FCSTD DOCUMENT  (FreeCAD 0.18R16146 (Git))
Label: t-1
License: All rights reserved
LicenseURL: http://en.wikipedia.org/wiki/All_rights_reserved
objects: Sketcher::SketchObject×1, PartDesign::Body×1
note: 2 computed .brp shape members not serialized (recipe doc carries the construction recipe); baked Part::Feature solids carry a one-line shape summary decoded from their .brp

FEATURE [Sketcher::SketchObject] Sketch
  MapMode = 5
  Support = -> [XY_Plane]
  sketch-geometry (9):
    g0: LineSegment StartX=0 StartY=0 StartZ=0 EndX=100 EndY=0 EndZ=0
    g1: LineSegment StartX=100 StartY=0 StartZ=0 EndX=100 EndY=33 EndZ=0
    g2: LineSegment StartX=100 StartY=33 StartZ=0 EndX=0 EndY=33 EndZ=0
    g3: LineSegment StartX=0 StartY=33 StartZ=0 EndX=0 EndY=0 EndZ=0
    g4: LineSegment StartX=6.2 StartY=31 StartZ=0 EndX=95 EndY=31 EndZ=0
    g5: LineSegment StartX=95 StartY=31 StartZ=0 EndX=95 EndY=2 EndZ=0
    g6: LineSegment StartX=95 StartY=2 StartZ=0 EndX=6.2 EndY=2 EndZ=0
    g7: LineSegment StartX=6.2 StartY=2 StartZ=0 EndX=6.2 EndY=31 EndZ=0
    g8: Circle CenterX=3.1 CenterY=29.9 CenterZ=0 NormalX=0 NormalY=0 NormalZ=1 AngleXU=0 Radius=1
  constraints (25):
    c: Coincident(g0,g1)
    c: Coincident(g1,g2)
    c: Coincident(g2,g3)
    c: Horizontal(g0)
    c: Horizontal(g2)
    c: Vertical(g1)
    c: Vertical(g3)
    c: Coincident(g0,g-1)
    c: DistanceX(g2,g1) = 100
    c: DistanceY(g0,g1) = 33
    c: Coincident(g4,g5)
    c: Coincident(g5,g6)
    c: Coincident(g6,g7)
    c: Coincident(g7,g4)
    c: Horizontal(g4)
    c: Horizontal(g6)
    c: Vertical(g5)
    c: Vertical(g7)
    c: DistanceY(g0,g6) = 2
    c: DistanceY(g4,g2) = 2
    c: DistanceX(g0,g6) = 6.2
    c: DistanceX(g5,g0) = 5
    c: Radius(g8) = 1
    c: DistanceX(g2,g8) = 3.1
    c: DistanceY(g8,g2) = 3.1
FEATURE [PartDesign::Body] Body
  Group = -> [Sketch]
  Origin = -> Origin
